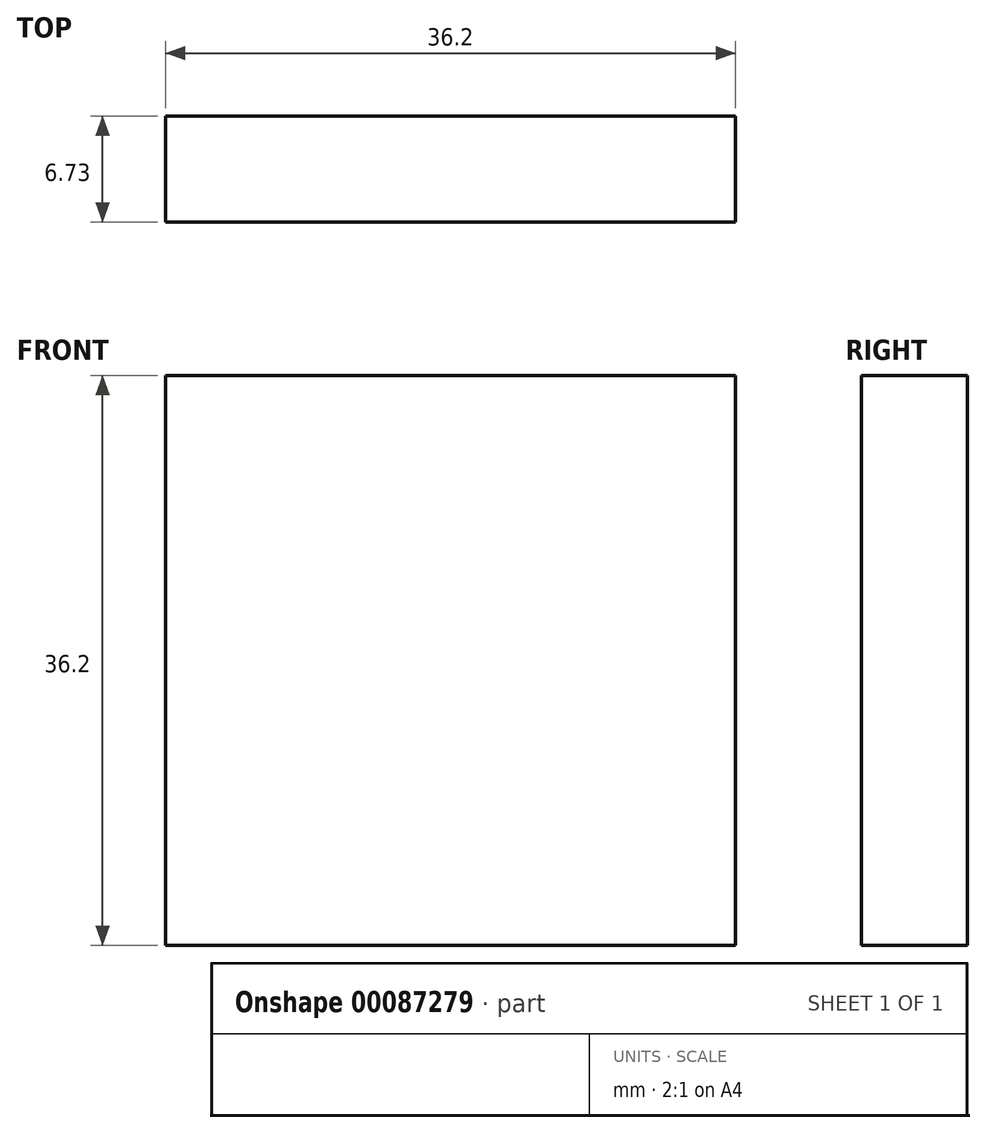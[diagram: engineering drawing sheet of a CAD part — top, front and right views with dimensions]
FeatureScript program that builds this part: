
annotation { "Feature Type Name" : "Feature", "Feature Type Description" : "" }
export const myFeature = defineFeature(function(context is Context, id is Id, definition is map)
    precondition{}
    {
        {
            var Q0;
            Q0=qCreatedBy(makeId("Front.planeOp"),FACE);
            var sketch = newSketch(context, id + "F0", { "sketchPlane" : qUnion([Q0])});
            skLineSegment(sketch, "E0.bottom", {"start": v(0, 0) * mm, "end": v(36.2, 0) * mm});
            skLineSegment(sketch, "E0.top", {"start": v(0, 36.2) * mm, "end": v(36.2, 36.2) * mm});
            skLineSegment(sketch, "E0.left", {"start": v(0, 0) * mm, "end": v(0, 36.2) * mm});
            skLineSegment(sketch, "E0.right", {"start": v(36.2, 0) * mm, "end": v(36.2, 36.2) * mm});
            skSolve(sketch);
        }
        {
            var Q0;
            Q0=makeQuery(id+"F0.imprint","IMPRINT",FACE,{"disambiguationData":[TD([[makeQuery(id+"F0.imprint","IMPRINT",EDGE,{"derivedFrom":sQuery(id+"F0.wireOp",EDGE,"E0.bottom")}),1.0]])]});
            extrude(context, id + "F1", {"entities" : qUnion([Q0]), "depth" : 6.73 * mm});
        }
    });
